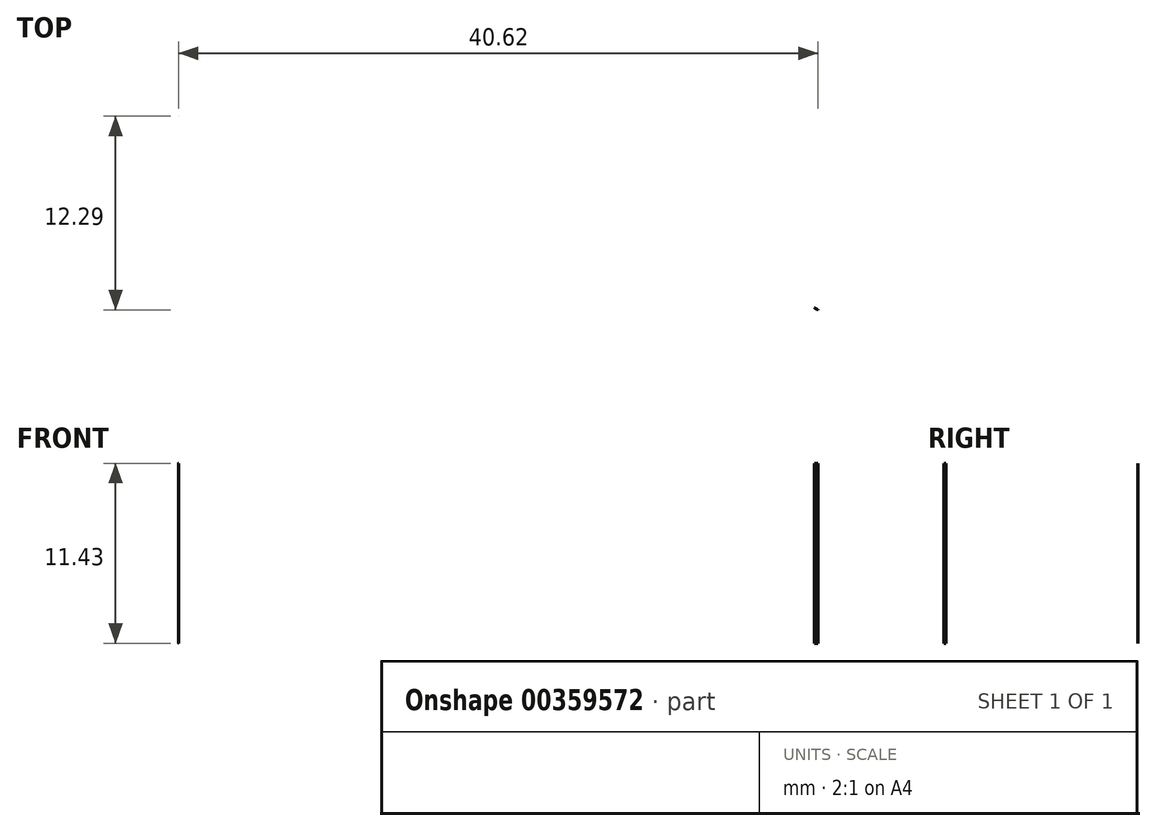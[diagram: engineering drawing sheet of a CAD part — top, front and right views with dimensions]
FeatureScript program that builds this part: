
annotation { "Feature Type Name" : "Feature", "Feature Type Description" : "" }
export const myFeature = defineFeature(function(context is Context, id is Id, definition is map)
    precondition{}
    {
        {
            var Q0;
            Q0=qCreatedBy(makeId("Top.planeOp"),FACE);
            var sketch = newSketch(context, id + "F0", { "sketchPlane" : qUnion([Q0])});
            skFitSpline(sketch, "E0", {"points": [v(0, -27.28) * mm, v(5.57, -21.36) * mm, v(8.53, -18.3) * mm, v(13, -14.44) * mm, v(17.13, -11.78) * mm, v(23.68, -7.77) * mm, v(33.43, -4.72) * mm, v(41.4, -2.75) * mm, v(45.44, -0.88) * mm, v(45.54, 2.87) * mm, v(29.03, 11.1) * mm, v(7.95, 17.42) * mm, v(3.03, 18.6) * mm, v(0, 18.83) * mm, v(0, 19.06) * mm], "startDerivative": vector(76.93, 81.72) * mm, "endDerivative": vector(7.39, 19.13) * mm});
            skFitSpline(sketch, "E1.MirrorCS", {"points": [v(0, -27.28) * mm, v(-5.57, -21.36) * mm, v(-8.53, -18.3) * mm, v(-13, -14.44) * mm, v(-17.13, -11.78) * mm, v(-23.68, -7.77) * mm, v(-33.43, -4.72) * mm, v(-41.4, -2.75) * mm, v(-45.44, -0.88) * mm, v(-45.54, 2.87) * mm, v(-29.03, 11.1) * mm, v(-7.95, 17.42) * mm, v(-3.03, 18.6) * mm, v(0, 18.83) * mm, v(0, 19.06) * mm], "startDerivative": vector(-76.93, 81.72) * mm, "endDerivative": vector(-7.39, 19.13) * mm});
            skFitSpline(sketch, "E2", {"points": [v(-2.04, -25.12) * mm, v(0, -25.8) * mm, v(2.04, -25.12) * mm], "startDerivative": vector(4.07, -2.03) * mm, "endDerivative": vector(4.07, 2.03) * mm});
            skFitSpline(sketch, "E3", {"points": [v(-0.38, 18.71) * mm, v(0, 18.75) * mm, v(0.36, 18.71) * mm, v(0.36, 18.71) * mm], "startDerivative": vector(0.72, 0.12) * mm, "endDerivative": vector(0.05, 0) * mm});
            skArc(sketch, "E4", {"start": v(-14.9, -4.17) * mm, "mid": v(0, -15.48) * mm, "end": v(14.9, -4.17) * mm});
            skFitSpline(sketch, "E5", {"points": [v(-12.44, 16.1) * mm, v(-14.9, 9.3) * mm, v(-15.42, 1.3) * mm], "startDerivative": vector(-6.06, -13.51) * mm, "endDerivative": vector(0.04, -16.04) * mm});
            skFitSpline(sketch, "E6.MirrorCS", {"points": [v(12.44, 16.1) * mm, v(14.9, 9.3) * mm, v(15.42, 1.3) * mm], "startDerivative": vector(6.06, -13.51) * mm, "endDerivative": vector(-0.04, -16.04) * mm});
            skArc(sketch, "E7", {"start": v(-14.9, 9.3) * mm, "mid": v(-16.03, 2.57) * mm, "end": v(-14.9, -4.17) * mm});
            skArc(sketch, "E8.MirrorCS", {"start": v(14.9, 9.3) * mm, "mid": v(16.03, 2.57) * mm, "end": v(14.9, -4.17) * mm});
            skArc(sketch, "E9", {"start": v(47.83, -3.3) * mm, "mid": v(59, 0.41) * mm, "end": v(49.11, 6.8) * mm});
            skArc(sketch, "E10", {"start": v(47.83, -3.3) * mm, "mid": v(45.38, -2.33) * mm, "end": v(42.74, -2.38) * mm});
            skArc(sketch, "E11", {"start": v(43.84, 5.54) * mm, "mid": v(45.7, 5.56) * mm, "end": v(47.53, 5.87) * mm});
            skCircle(sketch, "E12", {"center": v(52.52, 1.23) * mm, "radius": 1.5 * mm});
            skArc(sketch, "E13", {"start": v(40.76, 6.53) * mm, "mid": v(42.26, 5.9) * mm, "end": v(43.84, 5.54) * mm});
            skArc(sketch, "E14", {"start": v(47.53, 5.87) * mm, "mid": v(48.36, 6.27) * mm, "end": v(49.11, 6.8) * mm});
            skSolve(sketch);
        }
        {
            var Q0;
            Q0=makeQuery(id+"F0.imprint","IMPRINT",FACE,{"disambiguationData":[TD([[makeQuery(id+"F0.imprint","IMPRINT",EDGE,{"derivedFrom":sQuery(id+"F0.wireOp",EDGE,"E0")}),1.0]])]});
            extrude(context, id + "F1", {"entities" : qUnion([Q0]), "depth" : 11.43 * mm});
        }
    });
